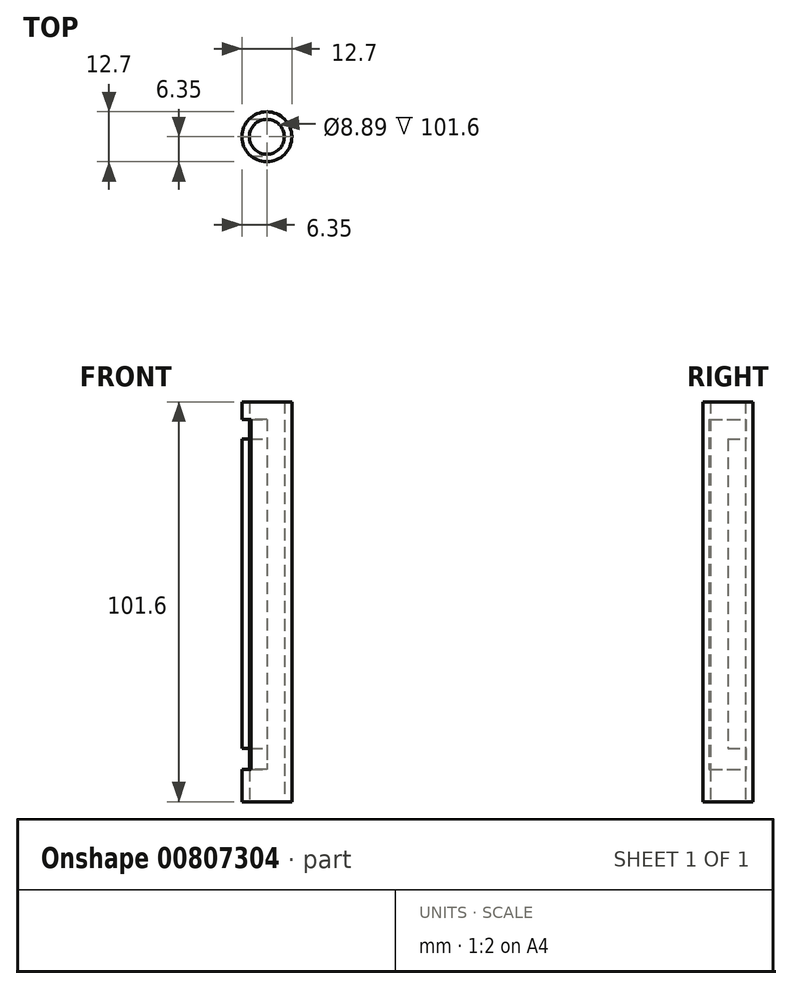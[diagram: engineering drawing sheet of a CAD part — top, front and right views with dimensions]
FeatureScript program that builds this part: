
annotation { "Feature Type Name" : "Feature", "Feature Type Description" : "" }
export const myFeature = defineFeature(function(context is Context, id is Id, definition is map)
    precondition{}
    {
        {
            var Q0;
            Q0=qCreatedBy(makeId("Top.planeOp"),FACE);
            var sketch = newSketch(context, id + "F0", { "sketchPlane" : qUnion([Q0])});
            skCircle(sketch, "E0", {"center": v(0, 0) * mm, "radius": 6.35 * mm});
            skCircle(sketch, "E1", {"center": v(0, 0) * mm, "radius": 4.45 * mm});
            skSolve(sketch);
        }
        {
            var Q0;
            Q0 = qSketchRegion(id + "F0", true);
            extrude(context, id + "F1", {"entities" : qUnion([Q0]), "depth" : 101.6 * mm, "offsetDistance" : 25.4 * mm});
        }
        {
            var Q0;
            Q0=qCreatedBy(makeId("Right.planeOp"),FACE);
            var sketch = newSketch(context, id + "F2", { "sketchPlane" : qUnion([Q0])});
            skLineSegment(sketch, "E2.bottom", {"start": v(0, 8.18) * mm, "end": v(0, 8.18) * mm});
            skLineSegment(sketch, "E2.top", {"start": v(0, 97.18) * mm, "end": v(0, 97.18) * mm});
            skLineSegment(sketch, "E3.bottom", {"start": v(0, 8.18) * mm, "end": v(4.52, 8.18) * mm});
            skLineSegment(sketch, "E3.top", {"start": v(0, 13.6) * mm, "end": v(4.52, 13.6) * mm});
            skLineSegment(sketch, "E3.left", {"start": v(0, 8.18) * mm, "end": v(0, 13.6) * mm});
            skLineSegment(sketch, "E3.right", {"start": v(4.52, 8.18) * mm, "end": v(4.52, 13.6) * mm});
            skLineSegment(sketch, "E4.bottom", {"start": v(0, 92.12) * mm, "end": v(4.52, 92.12) * mm});
            skLineSegment(sketch, "E4.top", {"start": v(0, 97.18) * mm, "end": v(4.52, 97.18) * mm});
            skLineSegment(sketch, "E4.left", {"start": v(0, 92.12) * mm, "end": v(0, 97.18) * mm});
            skLineSegment(sketch, "E4.right", {"start": v(4.52, 92.12) * mm, "end": v(4.52, 97.18) * mm});
            skLineSegment(sketch, "E5.bottom", {"start": v(0, 8.18) * mm, "end": v(-4.88, 8.18) * mm});
            skLineSegment(sketch, "E5.top", {"start": v(0, 97.18) * mm, "end": v(-4.88, 97.18) * mm});
            skLineSegment(sketch, "E5.left", {"start": v(0, 8.18) * mm, "end": v(0, 97.18) * mm});
            skLineSegment(sketch, "E5.right", {"start": v(-4.88, 8.18) * mm, "end": v(-4.88, 97.18) * mm});
            skSolve(sketch);
        }
        {
            var Q0;
            Q0 = qSketchRegion(id + "F2", true);
            extrude(context, id + "F3", {"entities" : qUnion([Q0]), "operationType" : NewBodyOperationType.REMOVE, "oppositeDirection" : true, "depth" : 25.4 * mm, "offsetDistance" : 25.4 * mm});
        }
    });
